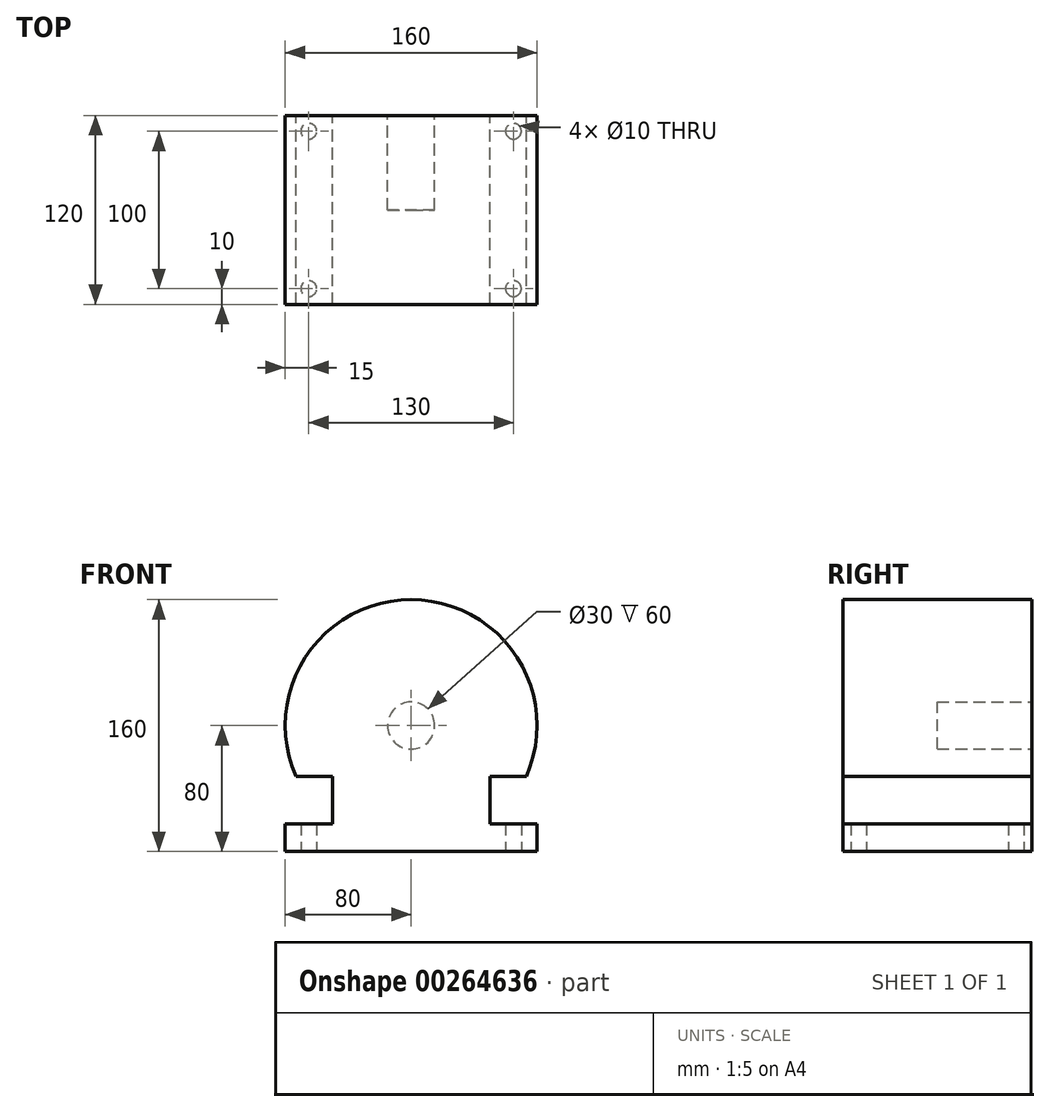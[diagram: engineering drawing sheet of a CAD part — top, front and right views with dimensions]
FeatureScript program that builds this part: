
annotation { "Feature Type Name" : "Feature", "Feature Type Description" : "" }
export const myFeature = defineFeature(function(context is Context, id is Id, definition is map)
    precondition{}
    {
        {
            var Q0;
            Q0=qCreatedBy(makeId("Front.planeOp"),FACE);
            var sketch = newSketch(context, id + "F0", { "sketchPlane" : qUnion([Q0])});
            skLineSegment(sketch, "E0", {"start": v(0, 0) * mm, "end": v(80, 0) * mm});
            skLineSegment(sketch, "E1", {"start": v(80, 0) * mm, "end": v(80, 17.55) * mm});
            skLineSegment(sketch, "E2", {"start": v(80, 17.55) * mm, "end": v(50, 17.55) * mm});
            skArc(sketch, "E3", {"start": v(-50, 17.55) * mm, "mid": v(0, 0) * mm, "end": v(50, 17.55) * mm});
            skLineSegment(sketch, "E4", {"start": v(0, 0) * mm, "end": v(-80, 0) * mm});
            skLineSegment(sketch, "E5", {"start": v(-80, 0) * mm, "end": v(-80, 17.55) * mm});
            skLineSegment(sketch, "E6", {"start": v(-80, 17.55) * mm, "end": v(-50, 17.55) * mm});
            skLineSegment(sketch, "E7", {"start": v(-65, 17.55) * mm, "end": v(-65, 0) * mm});
            skLineSegment(sketch, "E8", {"start": v(65, 17.55) * mm, "end": v(65, 0) * mm});
            skCircle(sketch, "E9", {"center": v(0, 80) * mm, "radius": 15 * mm});
            skLineSegment(sketch, "E10", {"start": v(-50, 17.55) * mm, "end": v(-50, 47.55) * mm});
            skLineSegment(sketch, "E11", {"start": v(-50, 47.55) * mm, "end": v(-73.12, 47.55) * mm});
            skLineSegment(sketch, "E12", {"start": v(50, 17.55) * mm, "end": v(50, 47.55) * mm});
            skLineSegment(sketch, "E13", {"start": v(50, 47.55) * mm, "end": v(73.12, 47.55) * mm});
            skArc(sketch, "E14.trimOffspring", {"start": v(73.12, 47.55) * mm, "mid": v(0, 160) * mm, "end": v(-73.12, 47.55) * mm});
            skSolve(sketch);
        }
        {
            var Q0;
            Q0=qCreatedBy(makeId("Top.planeOp"),FACE);
            var sketch = newSketch(context, id + "F1", { "sketchPlane" : qUnion([Q0])});
            skLineSegment(sketch, "E15.bottom", {"start": v(-65, -50) * mm, "end": v(65, -50) * mm});
            skLineSegment(sketch, "E15.top", {"start": v(-65, 50) * mm, "end": v(65, 50) * mm});
            skLineSegment(sketch, "E15.left", {"start": v(-65, -50) * mm, "end": v(-65, 50) * mm});
            skLineSegment(sketch, "E15.right", {"start": v(65, -50) * mm, "end": v(65, 50) * mm});
            skPoint(sketch, "E15.middle", {"position": v(0, 0) * mm});
            skCircle(sketch, "E16", {"center": v(-65, -50) * mm, "radius": 5 * mm});
            skCircle(sketch, "E17", {"center": v(65, -50) * mm, "radius": 5 * mm});
            skCircle(sketch, "E18", {"center": v(65, 50) * mm, "radius": 5 * mm});
            skCircle(sketch, "E19", {"center": v(-65, 50) * mm, "radius": 5 * mm});
            skSolve(sketch);
        }
        {
            var Q0;
            {var subQ0=sQuery(id+"F0.wireOp",EDGE,"E5");Q0=makeQuery(id+"F0.imprint","IMPRINT",FACE,{"disambiguationData":[TD([[makeQuery(id+"F0.imprint","IMPRINT",EDGE,{"derivedFrom":subQ0}),-1.0]])]});}
            var Q1;
            {var subQ5=sQuery(id+"F0.wireOp",EDGE,"E7");Q1=makeQuery(id+"F0.imprint","IMPRINT",FACE,{"disambiguationData":[TD([[makeQuery(id+"F0.imprint","IMPRINT",EDGE,{"derivedFrom":subQ5}),1.0]])]});}
            var Q2;
            Q2=makeQuery(id+"F0.imprint","IMPRINT",FACE,{"disambiguationData":[TD([[makeQuery(id+"F0.imprint","IMPRINT",EDGE,{"derivedFrom":sQuery(id+"F0.wireOp",EDGE,"E9")}),-1.0]])]});
            var Q3;
            {var subQ3=sQuery(id+"F0.wireOp",EDGE,"E8");Q3=makeQuery(id+"F0.imprint","IMPRINT",FACE,{"disambiguationData":[TD([[makeQuery(id+"F0.imprint","IMPRINT",EDGE,{"derivedFrom":subQ3}),-1.0]])]});}
            var Q4;
            {var subQ0=sQuery(id+"F0.wireOp",EDGE,"E1");Q4=makeQuery(id+"F0.imprint","IMPRINT",FACE,{"disambiguationData":[TD([[makeQuery(id+"F0.imprint","IMPRINT",EDGE,{"derivedFrom":subQ0}),1.0]])]});}
            extrude(context, id + "F2", {"entities" : qUnion([Q0, Q1, Q2, Q3, Q4]), "endBound" : BoundingType.SYMMETRIC, "depth" : 120 * mm});
        }
        {
            var Q0;
            {var subQ0=sQuery(id+"F1.wireOp",EDGE,"E15.left");var subQ1=sQuery(id+"F1.wireOp",EDGE,"E15.top");var subQ2=makeQuery(id+"F1.imprint","INTERSECT",VERTEX,{"derivedFrom":[subQ1,subQ0]});Q0=makeQuery(id+"F1.imprint","IMPRINT",FACE,{"disambiguationData":[TD([[makeQuery(id+"F1.imprint","IMPRINT",EDGE,{"disambiguationData":[TD([[subQ2,-1.0]])],"derivedFrom":subQ1}),1.0]])]});}
            var Q1;
            {var subQ0=sQuery(id+"F1.wireOp",EDGE,"E15.left");var subQ1=sQuery(id+"F1.wireOp",EDGE,"E15.top");var subQ2=makeQuery(id+"F1.imprint","INTERSECT",VERTEX,{"derivedFrom":[subQ1,subQ0]});Q1=makeQuery(id+"F1.imprint","IMPRINT",FACE,{"disambiguationData":[TD([[makeQuery(id+"F1.imprint","IMPRINT",EDGE,{"disambiguationData":[TD([[subQ2,-1.0]])],"derivedFrom":subQ1}),-1.0]])]});}
            var Q2;
            {var subQ0=sQuery(id+"F1.wireOp",EDGE,"E15.left");var subQ1=sQuery(id+"F1.wireOp",EDGE,"E15.bottom");var subQ2=makeQuery(id+"F1.imprint","INTERSECT",VERTEX,{"derivedFrom":[subQ1,subQ0]});Q2=makeQuery(id+"F1.imprint","IMPRINT",FACE,{"disambiguationData":[TD([[makeQuery(id+"F1.imprint","IMPRINT",EDGE,{"disambiguationData":[TD([[subQ2,-1.0]])],"derivedFrom":subQ1}),1.0]])]});}
            var Q3;
            {var subQ0=sQuery(id+"F1.wireOp",EDGE,"E15.left");var subQ1=sQuery(id+"F1.wireOp",EDGE,"E15.bottom");var subQ2=makeQuery(id+"F1.imprint","INTERSECT",VERTEX,{"derivedFrom":[subQ1,subQ0]});Q3=makeQuery(id+"F1.imprint","IMPRINT",FACE,{"disambiguationData":[TD([[makeQuery(id+"F1.imprint","IMPRINT",EDGE,{"disambiguationData":[TD([[subQ2,-1.0]])],"derivedFrom":subQ1}),-1.0]])]});}
            var Q4;
            {var subQ0=sQuery(id+"F1.wireOp",EDGE,"E15.right");var subQ1=sQuery(id+"F1.wireOp",EDGE,"E15.top");var subQ2=makeQuery(id+"F1.imprint","INTERSECT",VERTEX,{"derivedFrom":[subQ1,subQ0]});Q4=makeQuery(id+"F1.imprint","IMPRINT",FACE,{"disambiguationData":[TD([[makeQuery(id+"F1.imprint","IMPRINT",EDGE,{"disambiguationData":[TD([[subQ2,1.0]])],"derivedFrom":subQ1}),-1.0]])]});}
            var Q5;
            {var subQ0=sQuery(id+"F1.wireOp",EDGE,"E15.right");var subQ1=sQuery(id+"F1.wireOp",EDGE,"E15.top");var subQ2=makeQuery(id+"F1.imprint","INTERSECT",VERTEX,{"derivedFrom":[subQ1,subQ0]});Q5=makeQuery(id+"F1.imprint","IMPRINT",FACE,{"disambiguationData":[TD([[makeQuery(id+"F1.imprint","IMPRINT",EDGE,{"disambiguationData":[TD([[subQ2,1.0]])],"derivedFrom":subQ1}),1.0]])]});}
            var Q6;
            {var subQ0=sQuery(id+"F1.wireOp",EDGE,"E15.right");var subQ1=sQuery(id+"F1.wireOp",EDGE,"E15.bottom");var subQ2=makeQuery(id+"F1.imprint","INTERSECT",VERTEX,{"derivedFrom":[subQ1,subQ0]});Q6=makeQuery(id+"F1.imprint","IMPRINT",FACE,{"disambiguationData":[TD([[makeQuery(id+"F1.imprint","IMPRINT",EDGE,{"disambiguationData":[TD([[subQ2,1.0]])],"derivedFrom":subQ1}),-1.0]])]});}
            var Q7;
            {var subQ0=sQuery(id+"F1.wireOp",EDGE,"E15.right");var subQ1=sQuery(id+"F1.wireOp",EDGE,"E15.bottom");var subQ2=makeQuery(id+"F1.imprint","INTERSECT",VERTEX,{"derivedFrom":[subQ1,subQ0]});Q7=makeQuery(id+"F1.imprint","IMPRINT",FACE,{"disambiguationData":[TD([[makeQuery(id+"F1.imprint","IMPRINT",EDGE,{"disambiguationData":[TD([[subQ2,1.0]])],"derivedFrom":subQ1}),1.0]])]});}
            extrude(context, id + "F3", {"entities" : qUnion([Q0, Q1, Q2, Q3, Q4, Q5, Q6, Q7]), "operationType" : NewBodyOperationType.REMOVE, "depth" : 25 * mm});
        }
        {
            var Q0;
            Q0=makeQuery(id+"F0.imprint","IMPRINT",FACE,{"disambiguationData":[TD([[makeQuery(id+"F0.imprint","IMPRINT",EDGE,{"derivedFrom":sQuery(id+"F0.wireOp",EDGE,"E9")}),1.0]])]});
            var Q1;
            Q1=makeQuery(id+"F2.opExtrude","CAP_FACE",FACE,{"disambiguationData":[OSD([sQuery(id+"F0.wireOp",EDGE,"E0"),sQuery(id+"F0.wireOp",EDGE,"E1"),sQuery(id+"F0.wireOp",EDGE,"E2"),sQuery(id+"F0.wireOp",EDGE,"E4"),sQuery(id+"F0.wireOp",EDGE,"E5"),sQuery(id+"F0.wireOp",EDGE,"E6"),sQuery(id+"F0.wireOp",EDGE,"E9"),sQuery(id+"F0.wireOp",EDGE,"E10"),sQuery(id+"F0.wireOp",EDGE,"E11"),sQuery(id+"F0.wireOp",EDGE,"E12"),sQuery(id+"F0.wireOp",EDGE,"E13"),sQuery(id+"F0.wireOp",EDGE,"E14.trimOffspring")])],"isStart":false});
            extrude(context, id + "F4", {"entities" : qUnion([Q0]), "operationType" : NewBodyOperationType.ADD, "endBound" : BoundingType.UP_TO_SURFACE, "endBoundEntityFace" : qUnion([Q1]), "depth" : 25 * mm});
        }
    });
